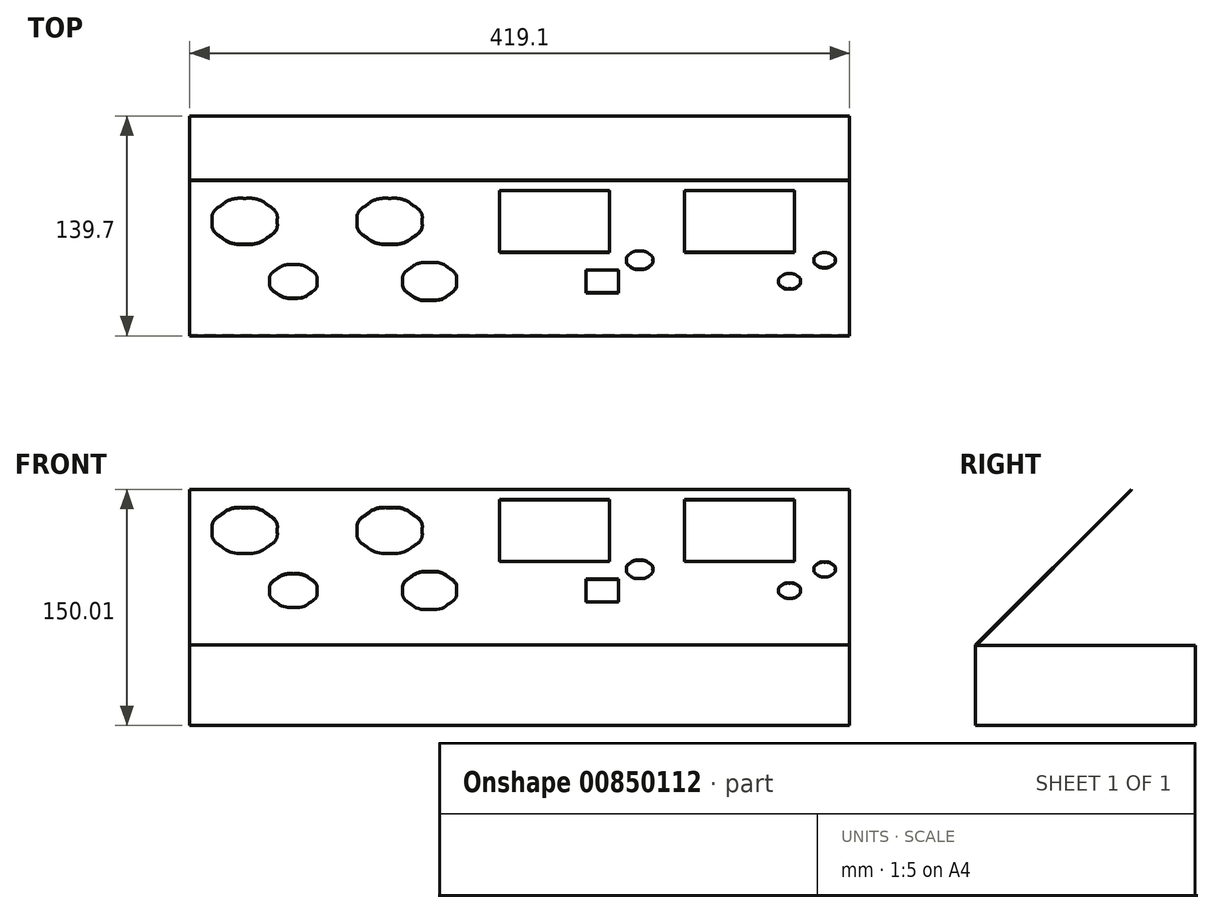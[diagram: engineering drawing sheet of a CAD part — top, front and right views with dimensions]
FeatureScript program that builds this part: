
annotation { "Feature Type Name" : "Feature", "Feature Type Description" : "" }
export const myFeature = defineFeature(function(context is Context, id is Id, definition is map)
    precondition{}
    {
        {
            var Q0;
            Q0=qCreatedBy(makeId("Right.planeOp"),FACE);
            var sketch = newSketch(context, id + "F0", { "sketchPlane" : qUnion([Q0])});
            skLineSegment(sketch, "E0.bottom", {"start": v(0, 0) * mm, "end": v(-139.7, 0) * mm});
            skLineSegment(sketch, "E0.top", {"start": v(0, 50.8) * mm, "end": v(-139.3, 50.8) * mm});
            skLineSegment(sketch, "E0.left", {"start": v(0, 0) * mm, "end": v(0, 50.8) * mm});
            skLineSegment(sketch, "E0.right", {"start": v(-139.7, 0) * mm, "end": v(-139.7, 51.22) * mm});
            skLineSegment(sketch, "E1", {"start": v(-139.7, 51.22) * mm, "end": v(-40.92, 150) * mm});
            skLineSegment(sketch, "E2", {"start": v(-40.92, 150) * mm, "end": v(-40.63, 149.72) * mm});
            skLineSegment(sketch, "E3", {"start": v(-40.63, 149.72) * mm, "end": v(-139.3, 51.05) * mm});
            skLineSegment(sketch, "E4", {"start": v(-139.3, 50.8) * mm, "end": v(-139.3, 51.05) * mm});
            skLineSegment(sketch, "E5", {"start": v(-139.3, 50.8) * mm, "end": v(-139.7, 50.8) * mm, "construction": true});
            skSolve(sketch);
        }
        {
            var Q0;
            Q0=qSketchRegion(id+"F0",true);
            extrude(context, id + "F1", {"entities" : qUnion([Q0]), "endBound" : BoundingType.SYMMETRIC, "depth" : 419.1 * mm, "offsetDistance" : 25.4 * mm});
        }
        {
            var Q0;
            Q0=makeQuery(id+"F1.opExtrude","SWEPT_FACE",FACE,{"disambiguationData":[OSD([sQuery(id+"F0.wireOp",EDGE,"E1")])]});
            var sketch = newSketch(context, id + "F2", { "sketchPlane" : qUnion([Q0])});
            skLineSegment(sketch, "E6", {"start": v(41.99, -24.01) * mm, "end": v(62.63, -24.01) * mm});
            skLineSegment(sketch, "E7", {"start": v(104.7, 68.06) * mm, "end": v(104.7, 12.5) * mm});
            skLineSegment(sketch, "E8", {"start": v(57.07, 12.5) * mm, "end": v(57.07, 68.06) * mm});
            skLineSegment(sketch, "E9", {"start": v(57.07, 68.06) * mm, "end": v(-12.78, 68.06) * mm});
            skLineSegment(sketch, "E10", {"start": v(-12.78, 68.06) * mm, "end": v(-12.78, 12.5) * mm});
            skLineSegment(sketch, "E11", {"start": v(-12.78, 12.5) * mm, "end": v(57.07, 12.5) * mm});
            skLineSegment(sketch, "E12", {"start": v(41.99, -3.37) * mm, "end": v(62.63, -3.37) * mm});
            skLineSegment(sketch, "E13", {"start": v(41.99, -3.37) * mm, "end": v(41.99, -24.01) * mm});
            skLineSegment(sketch, "E14", {"start": v(62.63, -24.01) * mm, "end": v(62.63, -3.37) * mm});
            skLineSegment(sketch, "E15", {"start": v(-209.63, -61.32) * mm, "end": v(-209.63, 77.6) * mm, "construction": true});
            skLineSegment(sketch, "E16", {"start": v(174.55, 12.5) * mm, "end": v(174.55, 68.06) * mm});
            skLineSegment(sketch, "E17", {"start": v(209.47, -61.32) * mm, "end": v(209.47, 77.6) * mm, "construction": true});
            skLineSegment(sketch, "E18", {"start": v(104.7, 12.5) * mm, "end": v(174.55, 12.5) * mm});
            skLineSegment(sketch, "E19", {"start": v(174.55, 68.06) * mm, "end": v(104.7, 68.06) * mm});
            skLineSegment(sketch, "E20", {"start": v(209.47, -61.32) * mm, "end": v(-209.63, -61.32) * mm, "construction": true});
            skLineSegment(sketch, "E21", {"start": v(-209.63, 77.6) * mm, "end": v(209.47, 77.6) * mm, "construction": true});
            skFitSpline(sketch, "E22", {"points": [v(-57.23, 3.37) * mm, v(-61.7, 3.37) * mm, v(-66.14, 1.53) * mm, v(-69.3, -1.62) * mm]});
            skFitSpline(sketch, "E23", {"points": [v(-69.3, -1.62) * mm, v(-72.46, -4.78) * mm, v(-74.3, -9.22) * mm, v(-74.3, -13.7) * mm, v(-74.3, -18.16) * mm, v(-72.46, -22.6) * mm, v(-69.3, -25.76) * mm]});
            skFitSpline(sketch, "E24", {"points": [v(-69.3, -25.76) * mm, v(-66.14, -28.92) * mm, v(-61.7, -30.76) * mm, v(-57.23, -30.76) * mm, v(-52.76, -30.76) * mm, v(-48.32, -28.92) * mm, v(-45.16, -25.76) * mm, v(-42, -22.6) * mm, v(-40.16, -18.16) * mm, v(-40.16, -13.7) * mm, v(-40.16, -9.22) * mm, v(-42, -4.78) * mm, v(-45.16, -1.62) * mm, v(-48.32, 1.53) * mm, v(-52.76, 3.37) * mm, v(-57.23, 3.37) * mm]});
            skFitSpline(sketch, "E25", {"points": [v(76.12, 13.7) * mm, v(73.94, 13.7) * mm, v(71.77, 12.8) * mm, v(70.23, 11.25) * mm]});
            skFitSpline(sketch, "E26", {"points": [v(70.23, 11.25) * mm, v(68.68, 9.7) * mm, v(67.79, 7.54) * mm, v(67.79, 5.36) * mm, v(67.79, 3.18) * mm, v(68.68, 1) * mm, v(70.23, -0.53) * mm]});
            skFitSpline(sketch, "E27", {"points": [v(70.23, -0.53) * mm, v(71.77, -2.08) * mm, v(73.94, -2.98) * mm, v(76.12, -2.98) * mm, v(78.3, -2.98) * mm, v(80.47, -2.08) * mm, v(82.01, -0.53) * mm]});
            skFitSpline(sketch, "E28", {"points": [v(82.01, -0.53) * mm, v(83.56, 1) * mm, v(84.46, 3.18) * mm, v(84.46, 5.36) * mm, v(84.46, 7.54) * mm, v(83.56, 9.7) * mm, v(82.01, 11.25) * mm]});
            skFitSpline(sketch, "E29", {"points": [v(82.01, 11.25) * mm, v(80.47, 12.8) * mm, v(78.3, 13.7) * mm, v(76.12, 13.7) * mm]});
            skFitSpline(sketch, "E30", {"points": [v(-82.63, 60.92) * mm, v(-88.03, 60.92) * mm, v(-93.4, 58.7) * mm, v(-97.22, 54.88) * mm]});
            skFitSpline(sketch, "E31", {"points": [v(-97.22, 54.88) * mm, v(-101.04, 51.06) * mm, v(-103.27, 45.69) * mm, v(-103.27, 40.28) * mm, v(-103.27, 34.88) * mm, v(-101.04, 29.51) * mm, v(-97.22, 25.7) * mm]});
            skFitSpline(sketch, "E32", {"points": [v(-97.22, 25.7) * mm, v(-93.4, 21.87) * mm, v(-88.03, 19.65) * mm, v(-82.63, 19.65) * mm, v(-77.23, 19.65) * mm, v(-71.86, 21.87) * mm, v(-68.04, 25.7) * mm]});
            skFitSpline(sketch, "E33", {"points": [v(-68.04, 25.7) * mm, v(-64.22, 29.51) * mm, v(-62, 34.88) * mm, v(-62, 40.28) * mm, v(-62, 45.69) * mm, v(-64.22, 51.06) * mm, v(-68.04, 54.88) * mm]});
            skFitSpline(sketch, "E34", {"points": [v(-68.04, 54.88) * mm, v(-71.86, 58.7) * mm, v(-77.23, 60.92) * mm, v(-82.63, 60.92) * mm]});
            skFitSpline(sketch, "E35", {"points": [v(-174.7, 60.92) * mm, v(-180.1, 60.92) * mm, v(-185.48, 58.7) * mm, v(-189.3, 54.88) * mm]});
            skFitSpline(sketch, "E36", {"points": [v(-189.3, 54.88) * mm, v(-193.12, 51.06) * mm, v(-195.34, 45.69) * mm, v(-195.34, 40.28) * mm, v(-195.34, 34.88) * mm, v(-193.12, 29.51) * mm, v(-189.3, 25.7) * mm]});
            skFitSpline(sketch, "E37", {"points": [v(-189.3, 25.7) * mm, v(-185.48, 21.87) * mm, v(-180.1, 19.65) * mm, v(-174.7, 19.65) * mm, v(-169.3, 19.65) * mm, v(-163.93, 21.87) * mm, v(-160.11, 25.7) * mm]});
            skFitSpline(sketch, "E38", {"points": [v(-160.11, 25.7) * mm, v(-156.3, 29.51) * mm, v(-154.07, 34.88) * mm, v(-154.07, 40.28) * mm, v(-154.07, 45.69) * mm, v(-156.3, 51.06) * mm, v(-160.11, 54.88) * mm]});
            skFitSpline(sketch, "E39", {"points": [v(-160.11, 54.88) * mm, v(-163.93, 58.7) * mm, v(-169.3, 60.92) * mm, v(-174.7, 60.92) * mm]});
            skFitSpline(sketch, "E40", {"points": [v(-143.78, 1.39) * mm, v(-147.73, 1.39) * mm, v(-151.66, -0.24) * mm, v(-154.45, -3.03) * mm]});
            skFitSpline(sketch, "E41", {"points": [v(-154.45, -3.03) * mm, v(-157.24, -5.82) * mm, v(-158.87, -9.74) * mm, v(-158.87, -13.7) * mm, v(-158.87, -17.64) * mm, v(-157.24, -21.56) * mm, v(-154.45, -24.36) * mm]});
            skFitSpline(sketch, "E42", {"points": [v(-154.45, -24.36) * mm, v(-151.66, -27.15) * mm, v(-147.73, -28.77) * mm, v(-143.78, -28.77) * mm, v(-139.84, -28.77) * mm, v(-135.91, -27.15) * mm, v(-133.12, -24.36) * mm, v(-130.33, -21.56) * mm, v(-128.7, -17.64) * mm, v(-128.7, -13.7) * mm, v(-128.7, -9.74) * mm, v(-130.33, -5.82) * mm, v(-133.12, -3.03) * mm]});
            skFitSpline(sketch, "E43", {"points": [v(-133.12, -3.03) * mm, v(-135.91, -0.24) * mm, v(-139.84, 1.39) * mm, v(-143.78, 1.39) * mm]});
            skFitSpline(sketch, "E44", {"points": [v(171.37, -6.75) * mm, v(169.55, -6.75) * mm, v(167.75, -7.5) * mm, v(166.46, -8.78) * mm]});
            skFitSpline(sketch, "E45", {"points": [v(166.46, -8.78) * mm, v(165.17, -10.07) * mm, v(164.43, -11.87) * mm, v(164.43, -13.7) * mm, v(164.43, -15.5) * mm, v(165.17, -17.32) * mm, v(166.46, -18.6) * mm]});
            skFitSpline(sketch, "E46", {"points": [v(166.46, -18.6) * mm, v(167.75, -19.89) * mm, v(169.55, -20.64) * mm, v(171.37, -20.64) * mm, v(173.19, -20.64) * mm, v(175, -19.89) * mm, v(176.28, -18.6) * mm, v(177.57, -17.32) * mm, v(178.32, -15.5) * mm, v(178.32, -13.7) * mm, v(178.32, -11.87) * mm, v(177.57, -10.07) * mm, v(176.28, -8.78) * mm]});
            skFitSpline(sketch, "E47", {"points": [v(176.28, -8.78) * mm, v(175, -7.5) * mm, v(173.19, -6.75) * mm, v(171.37, -6.75) * mm]});
            skFitSpline(sketch, "E48", {"points": [v(193.6, 12.1) * mm, v(191.83, 12.1) * mm, v(190.07, 11.38) * mm, v(188.82, 10.13) * mm]});
            skFitSpline(sketch, "E49", {"points": [v(188.82, 10.13) * mm, v(187.58, 8.88) * mm, v(186.85, 7.12) * mm, v(186.85, 5.36) * mm, v(186.85, 3.6) * mm, v(187.58, 1.84) * mm, v(188.82, 0.59) * mm]});
            skFitSpline(sketch, "E50", {"points": [v(188.82, 0.59) * mm, v(190.07, -0.66) * mm, v(191.83, -1.39) * mm, v(193.6, -1.39) * mm, v(195.36, -1.39) * mm, v(197.12, -0.66) * mm, v(198.37, 0.59) * mm]});
            skFitSpline(sketch, "E51", {"points": [v(198.37, 0.59) * mm, v(199.62, 1.84) * mm, v(200.34, 3.6) * mm, v(200.34, 5.36) * mm, v(200.34, 7.12) * mm, v(199.62, 8.88) * mm, v(198.37, 10.13) * mm]});
            skFitSpline(sketch, "E52", {"points": [v(198.37, 10.13) * mm, v(197.12, 11.38) * mm, v(195.36, 12.1) * mm, v(193.6, 12.1) * mm]});
            skSolve(sketch);
        }
        {
            var Q0;
            Q0=qSketchRegion(id+"F2",true);
            var Q1;
            Q1=makeQuery(id+"F1.opExtrude","SWEPT_FACE",FACE,{"disambiguationData":[OSD([sQuery(id+"F0.wireOp",EDGE,"E3")])]});
            extrude(context, id + "F3", {"entities" : qUnion([Q0]), "operationType" : NewBodyOperationType.REMOVE, "endBound" : BoundingType.UP_TO_SURFACE, "oppositeDirection" : true, "depth" : 25.4 * mm, "endBoundEntityFace" : qUnion([Q1]), "offsetDistance" : 25.4 * mm});
        }
    });
